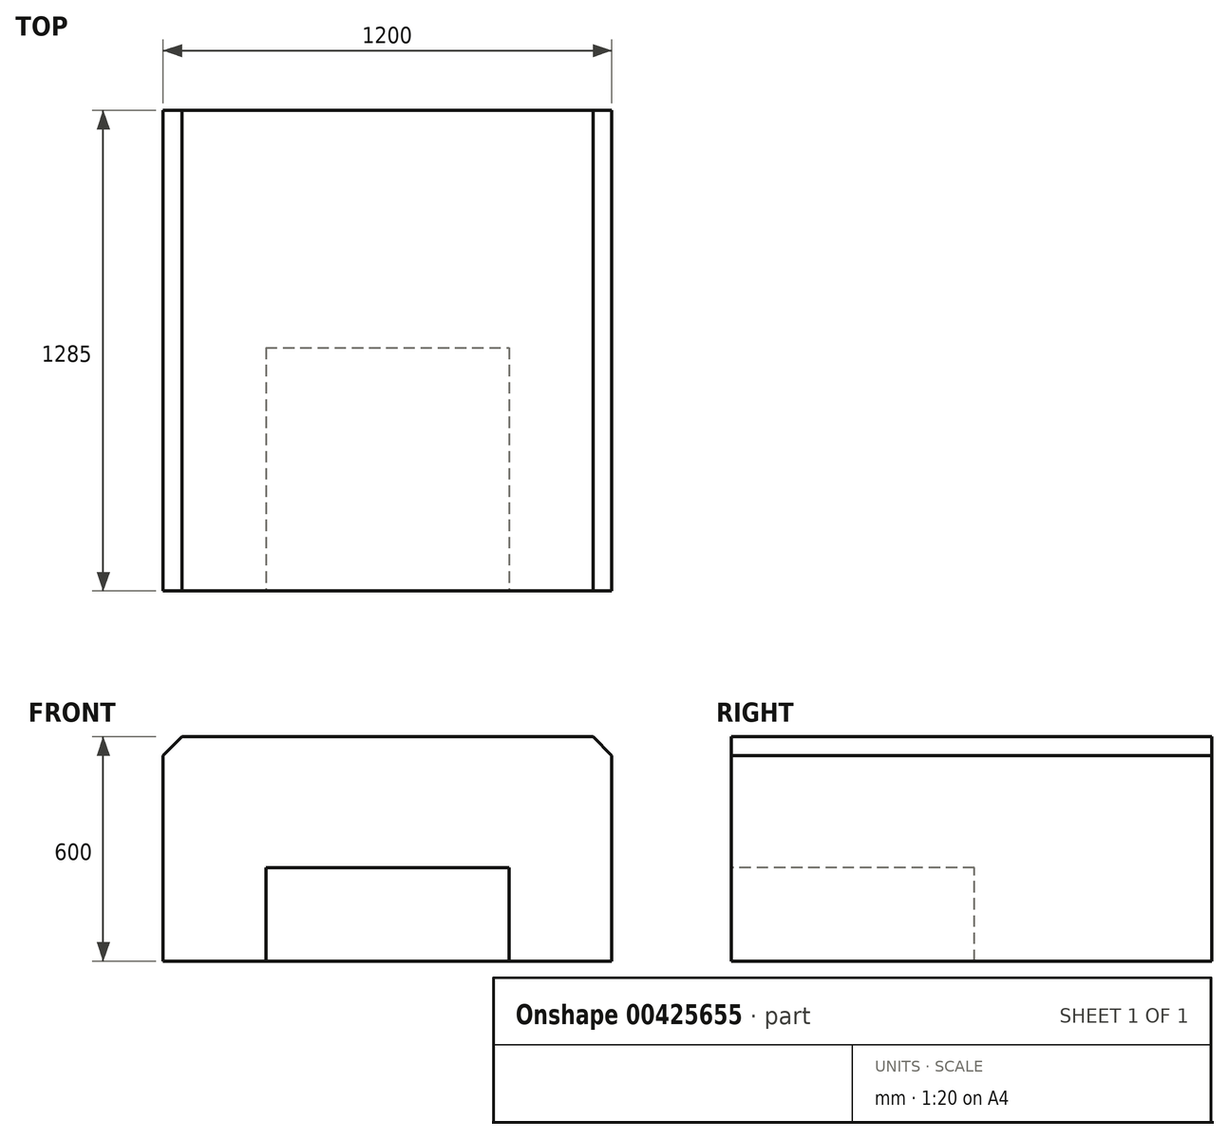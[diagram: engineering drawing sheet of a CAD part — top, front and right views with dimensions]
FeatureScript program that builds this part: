
annotation { "Feature Type Name" : "Feature", "Feature Type Description" : "" }
export const myFeature = defineFeature(function(context is Context, id is Id, definition is map)
    precondition{}
    {
        {
            var Q0;
            Q0=qCreatedBy(makeId("Front.planeOp"),FACE);
            var sketch = newSketch(context, id + "F0", { "sketchPlane" : qUnion([Q0])});
            skLineSegment(sketch, "E0", {"start": v(0, 0) * mm, "end": v(600, 0) * mm});
            skLineSegment(sketch, "E1", {"start": v(600, 0) * mm, "end": v(600, 550) * mm});
            skLineSegment(sketch, "E2", {"start": v(600, 550) * mm, "end": v(550, 600) * mm});
            skLineSegment(sketch, "E3", {"start": v(550, 600) * mm, "end": v(-550, 600) * mm});
            skLineSegment(sketch, "E4", {"start": v(-550, 600) * mm, "end": v(-600, 550) * mm});
            skLineSegment(sketch, "E5", {"start": v(-600, 550) * mm, "end": v(-600, 0) * mm});
            skLineSegment(sketch, "E6", {"start": v(-600, 0) * mm, "end": v(0, 0) * mm});
            skLineSegment(sketch, "E7", {"start": v(0, 0) * mm, "end": v(0, 600) * mm, "construction": true});
            skSolve(sketch);
        }
        {
            var Q0;
            Q0=makeQuery(id+"F0.imprint","IMPRINT",FACE,{"disambiguationData":[TD([[makeQuery(id+"F0.imprint","IMPRINT",EDGE,{"derivedFrom":sQuery(id+"F0.wireOp",EDGE,"E0")}),1.0]])]});
            extrude(context, id + "F1", {"entities" : qUnion([Q0]), "depth" : 1285 * mm});
        }
        {
            var Q0;
            Q0=makeQuery(id+"F1.opExtrude","CAP_FACE",FACE,{"disambiguationData":[OSD([sQuery(id+"F0.wireOp",EDGE,"E0"),sQuery(id+"F0.wireOp",EDGE,"E1"),sQuery(id+"F0.wireOp",EDGE,"E2"),sQuery(id+"F0.wireOp",EDGE,"E3"),sQuery(id+"F0.wireOp",EDGE,"E4"),sQuery(id+"F0.wireOp",EDGE,"E5"),sQuery(id+"F0.wireOp",EDGE,"E6")])],"isStart":false});
            var sketch = newSketch(context, id + "F2", { "sketchPlane" : qUnion([Q0])});
            skLineSegment(sketch, "E8.bottom", {"start": v(-325, 0) * mm, "end": v(325, 0) * mm});
            skLineSegment(sketch, "E8.top", {"start": v(-325, 250) * mm, "end": v(325, 250) * mm});
            skLineSegment(sketch, "E8.left", {"start": v(-325, 0) * mm, "end": v(-325, 250) * mm});
            skLineSegment(sketch, "E8.right", {"start": v(325, 0) * mm, "end": v(325, 250) * mm});
            skLineSegment(sketch, "E9", {"start": v(0, 0) * mm, "end": v(0, 250) * mm, "construction": true});
            skSolve(sketch);
        }
        {
            var Q0;
            Q0=makeQuery(id+"F2.imprint","IMPRINT",FACE,{"disambiguationData":[TD([[makeQuery(id+"F2.imprint","IMPRINT",EDGE,{"derivedFrom":sQuery(id+"F2.wireOp",EDGE,"E8.bottom")}),1.0]])]});
            extrude(context, id + "F3", {"entities" : qUnion([Q0]), "operationType" : NewBodyOperationType.REMOVE, "oppositeDirection" : true, "depth" : 650 * mm});
        }
    });
